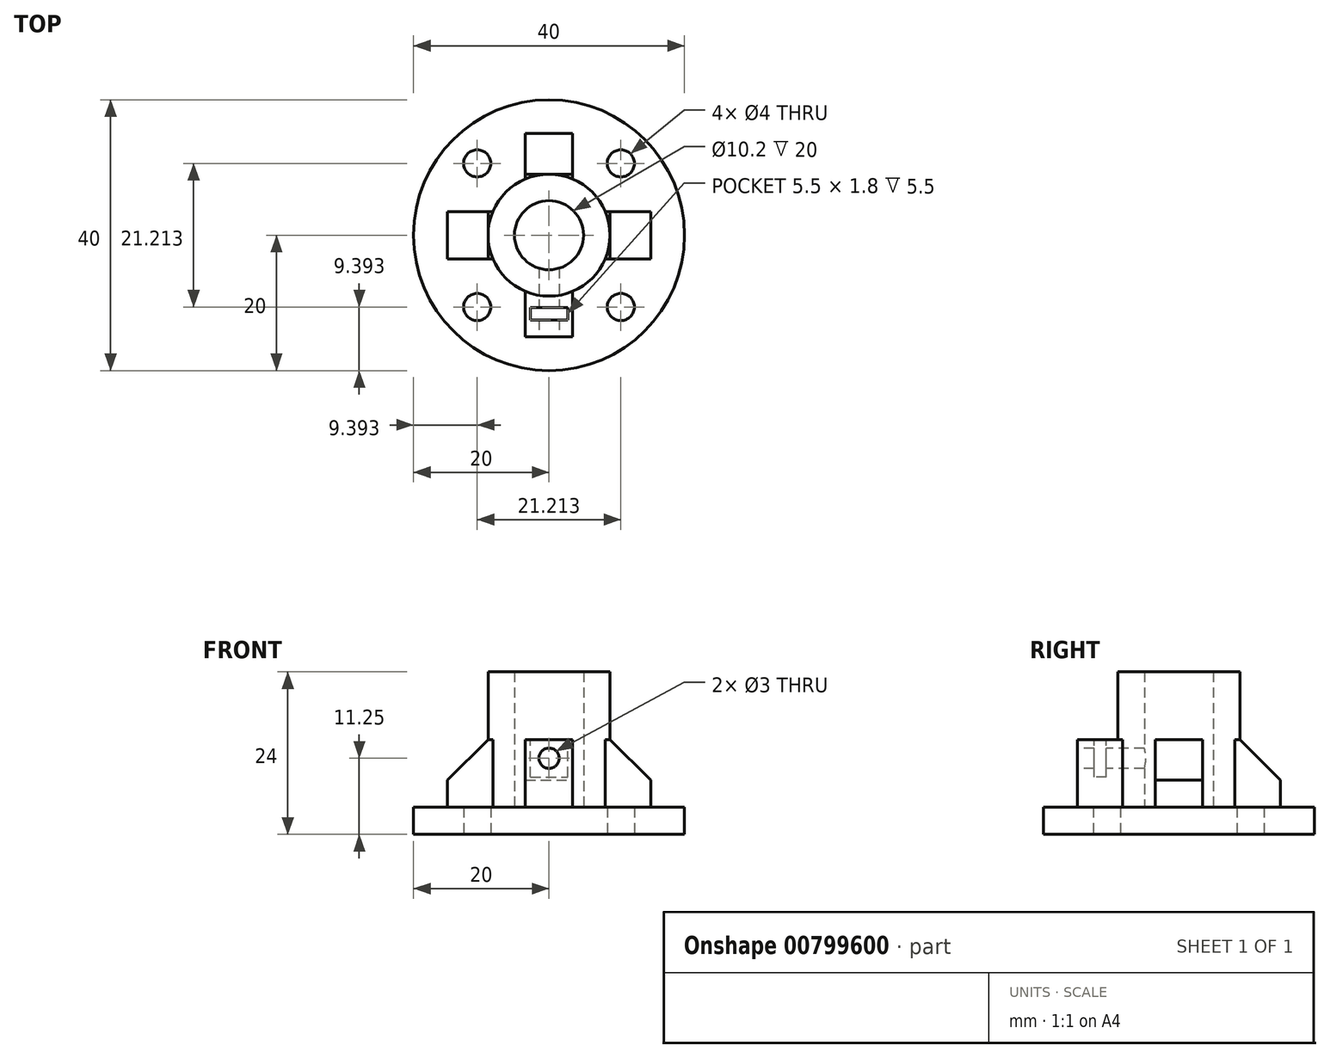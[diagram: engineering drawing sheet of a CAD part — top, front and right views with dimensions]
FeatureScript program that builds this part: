
annotation { "Feature Type Name" : "Feature", "Feature Type Description" : "" }
export const myFeature = defineFeature(function(context is Context, id is Id, definition is map)
    precondition{}
    {
        {
            var Q0;
            Q0=qCreatedBy(makeId("Top.planeOp"),FACE);
            var sketch = newSketch(context, id + "F0", { "sketchPlane" : qUnion([Q0])});
            skCircle(sketch, "E0", {"center": v(0, 0) * mm, "radius": 20 * mm});
            skSolve(sketch);
        }
        {
            var Q0;
            Q0=makeQuery(id+"F0.imprint","IMPRINT",FACE,{"disambiguationData":[TD([[makeQuery(id+"F0.imprint","IMPRINT",EDGE,{"derivedFrom":sQuery(id+"F0.wireOp",EDGE,"E0")}),1.0]])]});
            extrude(context, id + "F1", {"entities" : qUnion([Q0]), "depth" : 4 * mm, "offsetDistance" : 25 * mm});
        }
        {
            var Q0;
            Q0=makeQuery(id+"F1.opExtrude","CAP_FACE",FACE,{"disambiguationData":[OSD([sQuery(id+"F0.wireOp",EDGE,"E0")])],"isStart":false});
            var sketch = newSketch(context, id + "F2", { "sketchPlane" : qUnion([Q0])});
            skCircle(sketch, "E1", {"center": v(0, 0) * mm, "radius": 5.1 * mm});
            skCircle(sketch, "E2", {"center": v(0, 0) * mm, "radius": 9 * mm});
            skSolve(sketch);
        }
        {
            var Q0;
            Q0=makeQuery(id+"F2.imprint","IMPRINT",FACE,{"disambiguationData":[TD([[makeQuery(id+"F2.imprint","IMPRINT",EDGE,{"derivedFrom":sQuery(id+"F2.wireOp",EDGE,"E1")}),-1.0]])]});
            extrude(context, id + "F3", {"entities" : qUnion([Q0]), "operationType" : NewBodyOperationType.ADD, "depth" : 20 * mm, "offsetDistance" : 25 * mm});
        }
        {
            var Q0;
            {var subQ0=sQuery(id+"F0.wireOp",EDGE,"E0");Q0=makeQuery(id+"F3.boolean.opBoolean","SPLIT",FACE,{"disambiguationData":[TD([makeQuery(id+"F1.opExtrude","SWEPT_FACE",FACE,{"disambiguationData":[OSD([subQ0])]})])],"derivedFrom":makeQuery(id+"F1.opExtrude","CAP_FACE",FACE,{"disambiguationData":[OSD([subQ0])],"isStart":false})});}
            var sketch = newSketch(context, id + "F4", { "sketchPlane" : qUnion([Q0])});
            skLineSegment(sketch, "E3.bottom", {"start": v(-15, 3.5) * mm, "end": v(15, 3.5) * mm});
            skLineSegment(sketch, "E3.top", {"start": v(-15, -3.5) * mm, "end": v(15, -3.5) * mm});
            skLineSegment(sketch, "E3.left", {"start": v(-15, 3.5) * mm, "end": v(-15, -3.5) * mm});
            skLineSegment(sketch, "E3.right", {"start": v(15, 3.5) * mm, "end": v(15, -3.5) * mm});
            skLineSegment(sketch, "E4.bottom", {"start": v(-3.5, 15) * mm, "end": v(3.5, 15) * mm});
            skLineSegment(sketch, "E4.top", {"start": v(-3.5, -15) * mm, "end": v(3.5, -15) * mm});
            skLineSegment(sketch, "E4.left", {"start": v(-3.5, 15) * mm, "end": v(-3.5, -15) * mm});
            skLineSegment(sketch, "E4.right", {"start": v(3.5, 15) * mm, "end": v(3.5, -15) * mm});
            skSolve(sketch);
        }
        {
            var Q0;
            {var subQ0=sQuery(id+"F4.wireOp",EDGE,"E4.bottom");Q0=makeQuery(id+"F4.imprint","IMPRINT",FACE,{"disambiguationData":[TD([[makeQuery(id+"F4.imprint","IMPRINT",EDGE,{"derivedFrom":subQ0}),-1.0]])]});}
            var Q1;
            {var subQ0=sQuery(id+"F4.wireOp",EDGE,"E3.right");Q1=makeQuery(id+"F4.imprint","IMPRINT",FACE,{"disambiguationData":[TD([[makeQuery(id+"F4.imprint","IMPRINT",EDGE,{"derivedFrom":subQ0}),-1.0]])]});}
            var Q2;
            {var subQ0=sQuery(id+"F4.wireOp",EDGE,"E3.left");Q2=makeQuery(id+"F4.imprint","IMPRINT",FACE,{"disambiguationData":[TD([[makeQuery(id+"F4.imprint","IMPRINT",EDGE,{"derivedFrom":subQ0}),1.0]])]});}
            var Q3;
            {var subQ0=sQuery(id+"F4.wireOp",EDGE,"E4.top");Q3=makeQuery(id+"F4.imprint","IMPRINT",FACE,{"disambiguationData":[TD([[makeQuery(id+"F4.imprint","IMPRINT",EDGE,{"derivedFrom":subQ0}),1.0]])]});}
            extrude(context, id + "F5", {"entities" : qUnion([Q0, Q1, Q2, Q3]), "operationType" : NewBodyOperationType.ADD, "depth" : 10 * mm, "offsetDistance" : 25 * mm});
        }
        {
            var Q0;
            Q0=makeQuery(id+"F5.opExtrude","CAP_FACE",FACE,{"disambiguationData":[OSD([sQuery(id+"F2.wireOp",EDGE,"E2"),sQuery(id+"F4.wireOp",EDGE,"E4.top"),sQuery(id+"F4.wireOp",EDGE,"E4.left"),sQuery(id+"F4.wireOp",EDGE,"E4.right")])],"isStart":false});
            var sketch = newSketch(context, id + "F6", { "sketchPlane" : qUnion([Q0])});
            skLineSegment(sketch, "E5.bottom", {"start": v(-2.75, -10.7) * mm, "end": v(2.75, -10.7) * mm});
            skLineSegment(sketch, "E5.top", {"start": v(-2.75, -12.5) * mm, "end": v(2.75, -12.5) * mm});
            skLineSegment(sketch, "E5.left", {"start": v(-2.75, -10.7) * mm, "end": v(-2.75, -12.5) * mm});
            skLineSegment(sketch, "E5.right", {"start": v(2.75, -10.7) * mm, "end": v(2.75, -12.5) * mm});
            skSolve(sketch);
        }
        {
            var Q0;
            Q0=makeQuery(id+"F6.imprint","IMPRINT",FACE,{"disambiguationData":[TD([[makeQuery(id+"F6.imprint","IMPRINT",EDGE,{"derivedFrom":sQuery(id+"F6.wireOp",EDGE,"E5.bottom")}),-1.0]])]});
            extrude(context, id + "F7", {"entities" : qUnion([Q0]), "operationType" : NewBodyOperationType.REMOVE, "oppositeDirection" : true, "depth" : 5.5 * mm, "offsetDistance" : 25 * mm});
        }
        {
            var Q0;
            Q0=makeQuery(id+"F5.opExtrude","SWEPT_FACE",FACE,{"disambiguationData":[OSD([sQuery(id+"F4.wireOp",EDGE,"E4.top")])]});
            var sketch = newSketch(context, id + "F8", { "sketchPlane" : qUnion([Q0])});
            skPoint(sketch, "E6", {"position": v(0, 11.25) * mm});
            skCircle(sketch, "E7", {"center": v(0, 11.25) * mm, "radius": 1.5 * mm});
            skSolve(sketch);
        }
        {
            var Q0;
            Q0=makeQuery(id+"F8.imprint","IMPRINT",FACE,{"disambiguationData":[TD([[makeQuery(id+"F8.imprint","IMPRINT",EDGE,{"derivedFrom":sQuery(id+"F8.wireOp",EDGE,"E7")}),1.0]])]});
            extrude(context, id + "F9", {"entities" : qUnion([Q0]), "operationType" : NewBodyOperationType.REMOVE, "oppositeDirection" : true, "depth" : 11 * mm, "offsetDistance" : 25 * mm});
        }
        {
            var Q0;
            Q0=makeQuery(id+"F5.opExtrude","CAP_EDGE",EDGE,{"disambiguationData":[OSD([sQuery(id+"F4.wireOp",EDGE,"E3.right")])],"isStart":false});
            var Q1;
            Q1=makeQuery(id+"F5.opExtrude","CAP_EDGE",EDGE,{"disambiguationData":[OSD([sQuery(id+"F4.wireOp",EDGE,"E4.bottom")])],"isStart":false});
            var Q2;
            Q2=makeQuery(id+"F5.opExtrude","CAP_EDGE",EDGE,{"disambiguationData":[OSD([sQuery(id+"F4.wireOp",EDGE,"E3.left")])],"isStart":false});
            chamfer(context, id + "F10", {"entities" : qUnion([Q0, Q1, Q2]), "width" : 6 * mm, "tangentPropagation" : true});
        }
        {
            var Q0;
            Q0=makeQuery(id+"F1.opExtrude","CAP_FACE",FACE,{"disambiguationData":[OSD([sQuery(id+"F0.wireOp",EDGE,"E0")])],"isStart":true});
            var sketch = newSketch(context, id + "F11", { "sketchPlane" : qUnion([Q0])});
            skCircle(sketch, "E8", {"center": v(0, 0) * mm, "radius": 15 * mm});
            skLineSegment(sketch, "E9", {"start": v(0, 15) * mm, "end": v(0, -15) * mm});
            skLineSegment(sketch, "E10", {"start": v(15, 0) * mm, "end": v(-15, 0) * mm});
            skLineSegment(sketch, "E11", {"start": v(-10.6, 10.6) * mm, "end": v(0, 0) * mm});
            skLineSegment(sketch, "E12", {"start": v(0, 0) * mm, "end": v(10.6, 10.6) * mm});
            skLineSegment(sketch, "E13", {"start": v(0, 0) * mm, "end": v(10.6, -10.6) * mm});
            skLineSegment(sketch, "E14", {"start": v(0, 0) * mm, "end": v(-10.6, -10.6) * mm});
            skCircle(sketch, "E15", {"center": v(10.6, 10.6) * mm, "radius": 2 * mm});
            skCircle(sketch, "E16", {"center": v(10.6, -10.6) * mm, "radius": 2 * mm});
            skCircle(sketch, "E17", {"center": v(-10.6, -10.6) * mm, "radius": 2 * mm});
            skCircle(sketch, "E18", {"center": v(-10.6, 10.6) * mm, "radius": 2 * mm});
            skSolve(sketch);
        }
        {
            var Q0;
            {var subQ0=sQuery(id+"F11.wireOp",EDGE,"E8");var subQ1=makeQuery(id+"F11.imprint","INTERSECT",VERTEX,{"derivedFrom":[subQ0,sQuery(id+"F11.wireOp",EDGE,"E11")]});Q0=makeQuery(id+"F11.imprint","IMPRINT",FACE,{"disambiguationData":[TD([[makeQuery(id+"F11.imprint","IMPRINT",EDGE,{"disambiguationData":[TD([[subQ1,1.0]])],"derivedFrom":subQ0}),-1.0]])]});}
            var Q1;
            {var subQ0=sQuery(id+"F11.wireOp",EDGE,"E11");var subQ1=sQuery(id+"F11.wireOp",EDGE,"E8");var subQ2=makeQuery(id+"F11.imprint","INTERSECT",VERTEX,{"derivedFrom":[subQ1,subQ0]});Q1=makeQuery(id+"F11.imprint","IMPRINT",FACE,{"disambiguationData":[TD([[makeQuery(id+"F11.imprint","IMPRINT",EDGE,{"disambiguationData":[TD([[subQ2,1.0]])],"derivedFrom":subQ1}),1.0]])]});}
            var Q2;
            {var subQ0=sQuery(id+"F11.wireOp",EDGE,"E11");var subQ1=sQuery(id+"F11.wireOp",EDGE,"E8");var subQ2=makeQuery(id+"F11.imprint","INTERSECT",VERTEX,{"derivedFrom":[subQ1,subQ0]});Q2=makeQuery(id+"F11.imprint","IMPRINT",FACE,{"disambiguationData":[TD([[makeQuery(id+"F11.imprint","IMPRINT",EDGE,{"disambiguationData":[TD([[subQ2,-1.0]])],"derivedFrom":subQ1}),1.0]])]});}
            var Q3;
            {var subQ0=sQuery(id+"F11.wireOp",EDGE,"E12");var subQ1=sQuery(id+"F11.wireOp",EDGE,"E8");var subQ2=makeQuery(id+"F11.imprint","INTERSECT",VERTEX,{"derivedFrom":[subQ1,subQ0]});Q3=makeQuery(id+"F11.imprint","IMPRINT",FACE,{"disambiguationData":[TD([[makeQuery(id+"F11.imprint","IMPRINT",EDGE,{"disambiguationData":[TD([[subQ2,1.0]])],"derivedFrom":subQ1}),1.0]])]});}
            var Q4;
            {var subQ0=sQuery(id+"F11.wireOp",EDGE,"E8");var subQ1=makeQuery(id+"F11.imprint","INTERSECT",VERTEX,{"derivedFrom":[subQ0,sQuery(id+"F11.wireOp",EDGE,"E12")]});Q4=makeQuery(id+"F11.imprint","IMPRINT",FACE,{"disambiguationData":[TD([[makeQuery(id+"F11.imprint","IMPRINT",EDGE,{"disambiguationData":[TD([[subQ1,1.0]])],"derivedFrom":subQ0}),-1.0]])]});}
            var Q5;
            {var subQ0=sQuery(id+"F11.wireOp",EDGE,"E12");var subQ1=sQuery(id+"F11.wireOp",EDGE,"E8");var subQ2=makeQuery(id+"F11.imprint","INTERSECT",VERTEX,{"derivedFrom":[subQ1,subQ0]});Q5=makeQuery(id+"F11.imprint","IMPRINT",FACE,{"disambiguationData":[TD([[makeQuery(id+"F11.imprint","IMPRINT",EDGE,{"disambiguationData":[TD([[subQ2,-1.0]])],"derivedFrom":subQ1}),1.0]])]});}
            var Q6;
            {var subQ0=sQuery(id+"F11.wireOp",EDGE,"E8");var subQ1=makeQuery(id+"F11.imprint","INTERSECT",VERTEX,{"derivedFrom":[subQ0,sQuery(id+"F11.wireOp",EDGE,"E13")]});Q6=makeQuery(id+"F11.imprint","IMPRINT",FACE,{"disambiguationData":[TD([[makeQuery(id+"F11.imprint","IMPRINT",EDGE,{"disambiguationData":[TD([[subQ1,1.0]])],"derivedFrom":subQ0}),-1.0]])]});}
            var Q7;
            {var subQ0=sQuery(id+"F11.wireOp",EDGE,"E13");var subQ1=sQuery(id+"F11.wireOp",EDGE,"E8");var subQ2=makeQuery(id+"F11.imprint","INTERSECT",VERTEX,{"derivedFrom":[subQ1,subQ0]});Q7=makeQuery(id+"F11.imprint","IMPRINT",FACE,{"disambiguationData":[TD([[makeQuery(id+"F11.imprint","IMPRINT",EDGE,{"disambiguationData":[TD([[subQ2,-1.0]])],"derivedFrom":subQ1}),1.0]])]});}
            var Q8;
            {var subQ0=sQuery(id+"F11.wireOp",EDGE,"E13");var subQ1=sQuery(id+"F11.wireOp",EDGE,"E8");var subQ2=makeQuery(id+"F11.imprint","INTERSECT",VERTEX,{"derivedFrom":[subQ1,subQ0]});Q8=makeQuery(id+"F11.imprint","IMPRINT",FACE,{"disambiguationData":[TD([[makeQuery(id+"F11.imprint","IMPRINT",EDGE,{"disambiguationData":[TD([[subQ2,1.0]])],"derivedFrom":subQ1}),1.0]])]});}
            var Q9;
            {var subQ0=sQuery(id+"F11.wireOp",EDGE,"E8");var subQ1=makeQuery(id+"F11.imprint","INTERSECT",VERTEX,{"derivedFrom":[subQ0,sQuery(id+"F11.wireOp",EDGE,"E14")]});Q9=makeQuery(id+"F11.imprint","IMPRINT",FACE,{"disambiguationData":[TD([[makeQuery(id+"F11.imprint","IMPRINT",EDGE,{"disambiguationData":[TD([[subQ1,1.0]])],"derivedFrom":subQ0}),-1.0]])]});}
            var Q10;
            {var subQ0=sQuery(id+"F11.wireOp",EDGE,"E14");var subQ1=sQuery(id+"F11.wireOp",EDGE,"E8");var subQ2=makeQuery(id+"F11.imprint","INTERSECT",VERTEX,{"derivedFrom":[subQ1,subQ0]});Q10=makeQuery(id+"F11.imprint","IMPRINT",FACE,{"disambiguationData":[TD([[makeQuery(id+"F11.imprint","IMPRINT",EDGE,{"disambiguationData":[TD([[subQ2,-1.0]])],"derivedFrom":subQ1}),1.0]])]});}
            var Q11;
            {var subQ0=sQuery(id+"F11.wireOp",EDGE,"E14");var subQ1=sQuery(id+"F11.wireOp",EDGE,"E8");var subQ2=makeQuery(id+"F11.imprint","INTERSECT",VERTEX,{"derivedFrom":[subQ1,subQ0]});Q11=makeQuery(id+"F11.imprint","IMPRINT",FACE,{"disambiguationData":[TD([[makeQuery(id+"F11.imprint","IMPRINT",EDGE,{"disambiguationData":[TD([[subQ2,1.0]])],"derivedFrom":subQ1}),1.0]])]});}
            extrude(context, id + "F12", {"entities" : qUnion([Q0, Q1, Q2, Q3, Q4, Q5, Q6, Q7, Q8, Q9, Q10, Q11]), "operationType" : NewBodyOperationType.REMOVE, "oppositeDirection" : true, "depth" : 25 * mm, "offsetDistance" : 25 * mm});
        }
    });
